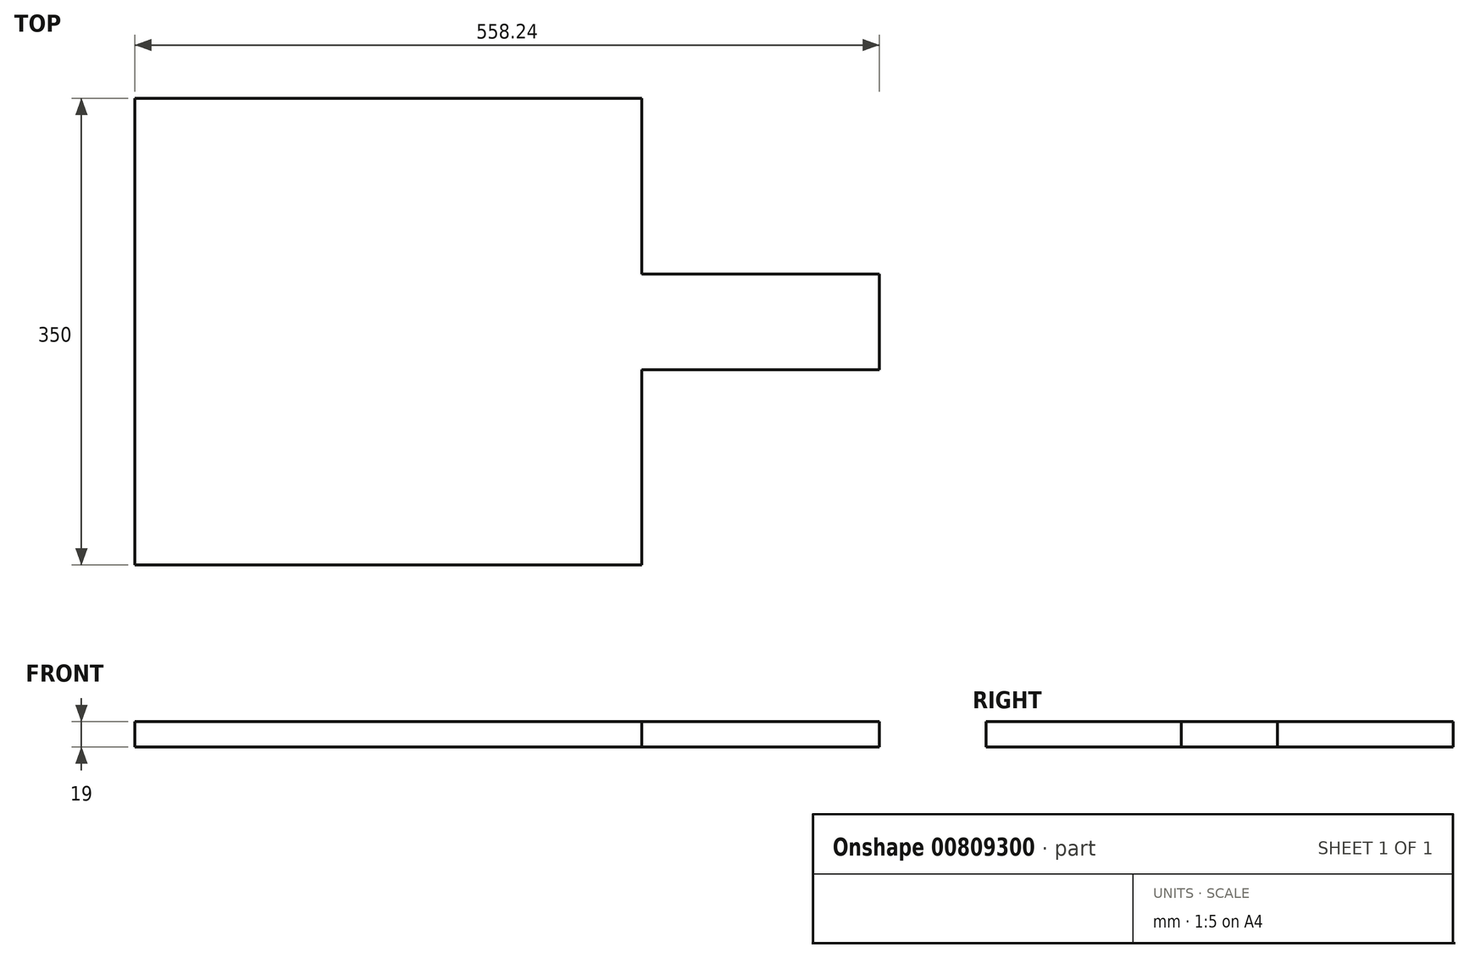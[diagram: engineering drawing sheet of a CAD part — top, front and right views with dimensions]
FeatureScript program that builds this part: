
annotation { "Feature Type Name" : "Feature", "Feature Type Description" : "" }
export const myFeature = defineFeature(function(context is Context, id is Id, definition is map)
    precondition{}
    {
        {
            var Q0;
            Q0=qCreatedBy(makeId("Top.planeOp"),FACE);
            var sketch = newSketch(context, id + "F0", { "sketchPlane" : qUnion([Q0])});
            skLineSegment(sketch, "E0.bottom", {"start": v(-31.33, -41.34) * mm, "end": v(348.67, -41.34) * mm});
            skLineSegment(sketch, "E0.top", {"start": v(-31.33, 308.66) * mm, "end": v(348.67, 308.66) * mm});
            skLineSegment(sketch, "E0.left", {"start": v(-31.33, -41.34) * mm, "end": v(-31.33, 308.66) * mm});
            skLineSegment(sketch, "E0.right", {"start": v(348.67, -41.34) * mm, "end": v(348.67, 104.91) * mm});
            skLineSegment(sketch, "E1.bottom", {"start": v(348.67, 104.91) * mm, "end": v(526.9, 104.91) * mm});
            skLineSegment(sketch, "E1.top", {"start": v(348.67, 176.92) * mm, "end": v(526.9, 176.92) * mm});
            skLineSegment(sketch, "E1.right", {"start": v(526.9, 104.91) * mm, "end": v(526.9, 176.92) * mm});
            skLineSegment(sketch, "E2.trimOffspring", {"start": v(348.67, 176.92) * mm, "end": v(348.67, 308.66) * mm});
            skSolve(sketch);
        }
        {
            var Q0;
            Q0 = qSketchRegion(id + "F0", true);
            extrude(context, id + "F1", {"entities" : qUnion([Q0]), "depth" : 19 * mm, "offsetDistance" : 25 * mm});
        }
    });
